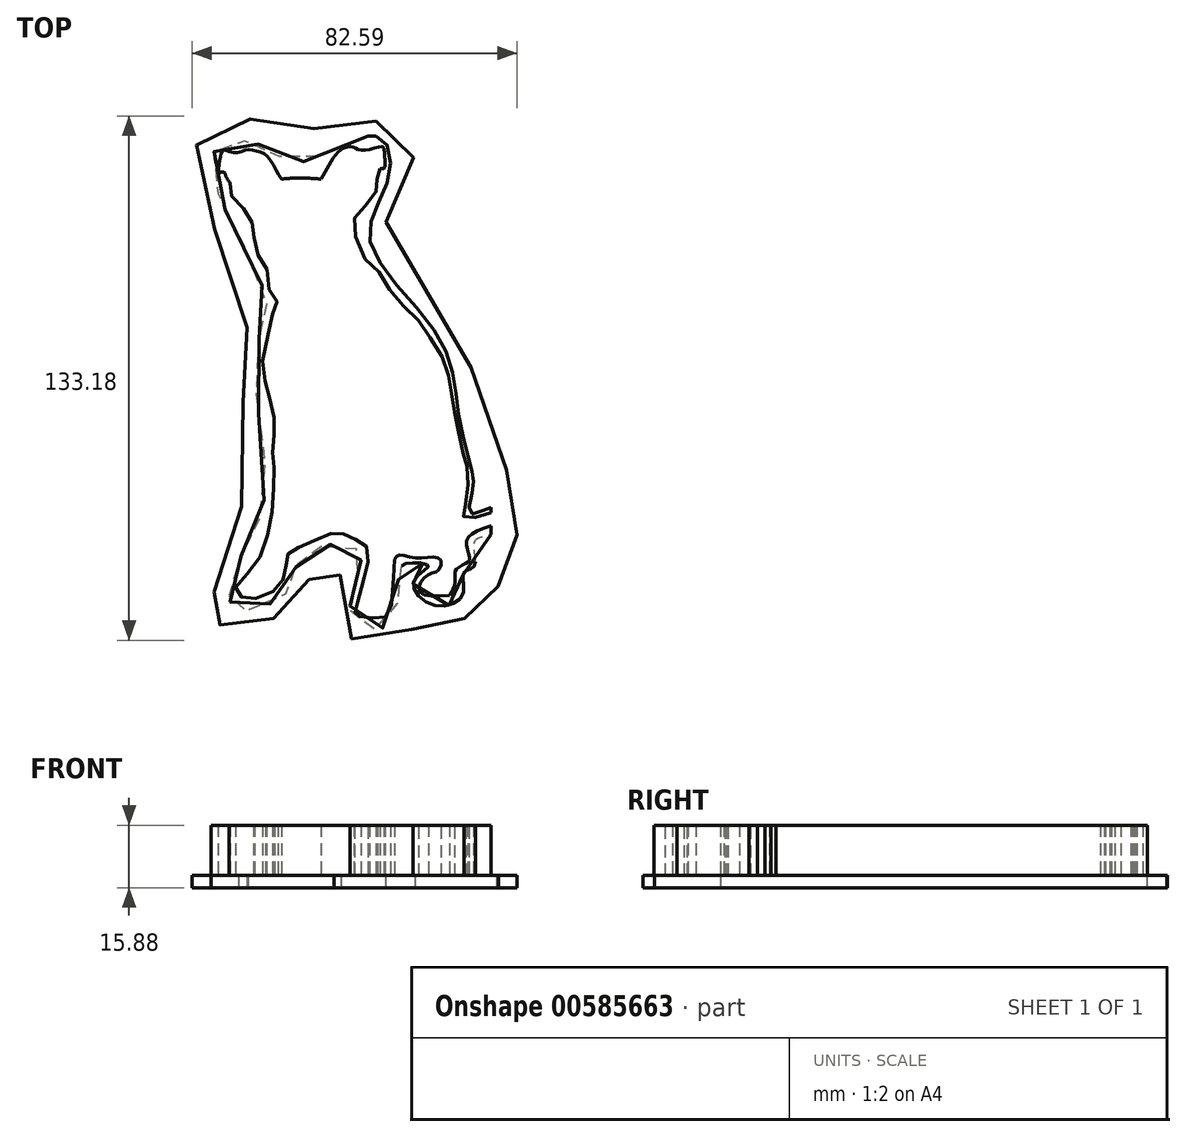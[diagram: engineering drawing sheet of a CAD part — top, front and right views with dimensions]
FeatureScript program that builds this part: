
annotation { "Feature Type Name" : "Feature", "Feature Type Description" : "" }
export const myFeature = defineFeature(function(context is Context, id is Id, definition is map)
    precondition{}
    {
        {
            var Q0;
            Q0=qCreatedBy(makeId("Top.planeOp"),FACE);
            var sketch = newSketch(context, id + "F0", { "sketchPlane" : qUnion([Q0])});
            skLineSegment(sketch, "E0.bottom", {"start": v(38.1, 63.5) * mm, "end": v(-38.1, 63.5) * mm});
            skLineSegment(sketch, "E0.top", {"start": v(38.1, -63.5) * mm, "end": v(-38.1, -63.5) * mm});
            skLineSegment(sketch, "E0.left", {"start": v(38.1, 63.5) * mm, "end": v(38.1, -63.5) * mm});
            skLineSegment(sketch, "E0.right", {"start": v(-38.1, 63.5) * mm, "end": v(-38.1, -63.5) * mm});
            skPoint(sketch, "E0.middle", {"position": v(0, 0) * mm});
            skFitSpline(sketch, "E1", {"points": [v(-26.8, -51.28) * mm, v(-24.47, -48.42) * mm, v(-21, -44.42) * mm, v(-18.8, -38.54) * mm, v(-17.53, -32.17) * mm, v(-17.04, -25.62) * mm, v(-16.95, -20.53) * mm, v(-17.3, -17.93) * mm, v(-17.22, -14.64) * mm, v(-16.87, -11.04) * mm, v(-17.17, -7.08) * mm, v(-18.27, -2.51) * mm, v(-19.15, 1.04) * mm, v(-19.9, 5.22) * mm, v(-18.45, 13.48) * mm, v(-17.35, 18.35) * mm, v(-15.94, 20.72) * mm, v(-17.17, 22.44) * mm, v(-18.27, 24.68) * mm, v(-18.67, 29.46) * mm, v(-20.56, 32.4) * mm, v(-22.05, 36.01) * mm, v(-22.1, 39.52) * mm, v(-22.7, 41.72) * mm, v(-24.17, 44.44) * mm, v(-27.15, 47.31) * mm, v(-28.2, 49.45) * mm, v(-28.2, 51.54) * mm], "startDerivative": vector(59.27, 78.39) * mm, "endDerivative": vector(6.28, 78.17) * mm});
            skFitSpline(sketch, "E2", {"points": [v(-28.2, 51.54) * mm, v(-29.08, 53) * mm, v(-29.7, 54.3) * mm, v(-31.17, 53.97) * mm], "startDerivative": vector(-2.88, 3.86) * mm, "endDerivative": vector(-5.2, -2.35) * mm});
            skFitSpline(sketch, "E3", {"points": [v(-31.17, 53.97) * mm, v(-30.85, 56.65) * mm, v(-30.45, 58.84) * mm, v(-29.9, 59.85) * mm, v(-27.97, 59.37) * mm, v(-25.6, 59.37) * mm, v(-23.7, 60) * mm, v(-21.4, 59.67) * mm, v(-19.33, 58.86) * mm, v(-17.13, 56) * mm, v(-15.12, 52.52) * mm], "startDerivative": vector(2.8, 25.68) * mm, "endDerivative": vector(15.15, -26.64) * mm});
            skFitSpline(sketch, "E4", {"points": [v(-15.12, 52.52) * mm, v(-10.78, 52.82) * mm, v(-5.05, 52.52) * mm], "startDerivative": vector(9, 0.91) * mm, "endDerivative": vector(11.08, -0.87) * mm});
            skFitSpline(sketch, "E5", {"points": [v(-5.05, 52.52) * mm, v(-2.66, 56.77) * mm, v(0, 59.98) * mm, v(2.96, 60.74) * mm, v(5.49, 59.8) * mm, v(10.43, 60.79) * mm, v(11, 60.3) * mm], "startDerivative": vector(11.4, 21.1) * mm, "endDerivative": vector(4.14, -8.3) * mm});
            skFitSpline(sketch, "E6", {"points": [v(11, 60.3) * mm, v(11.15, 57.78) * mm, v(11, 55.3) * mm, v(10.01, 55.23) * mm], "startDerivative": vector(0.31, -6.1) * mm, "endDerivative": vector(-4.87, 1.04) * mm});
            skFitSpline(sketch, "E7", {"points": [v(10.01, 55.23) * mm, v(9.2, 53.36) * mm, v(9.29, 50.86) * mm, v(8.39, 48.27) * mm, v(4.26, 43.68) * mm, v(3.36, 41.77) * mm, v(5.4, 33.2) * mm, v(9.77, 28.85) * mm, v(13.26, 23.1) * mm, v(18.64, 17.83) * mm, v(22.49, 12.64) * mm, v(26.42, 5.83) * mm, v(27.78, 0.19) * mm, v(28.58, -5.18) * mm, v(29.87, -11.33) * mm, v(31.3, -18.15) * mm, v(32.04, -20.73) * mm, v(32.19, -26.72) * mm, v(31.37, -31.45) * mm, v(31.3, -33.37) * mm, v(33.4, -33.62) * mm, v(36.62, -32.74) * mm, v(43.28, -30.45) * mm], "startDerivative": vector(-36.05, -59.29) * mm, "endDerivative": vector(133.24, 45.56) * mm});
            skFitSpline(sketch, "E8", {"points": [v(-26.8, -51.28) * mm, v(-24.66, -54) * mm, v(-17.08, -52.08) * mm, v(-14.04, -46.92) * mm, v(-13.48, -42.76) * mm, v(-8.7, -40.27) * mm, v(-1.18, -37.23) * mm, v(2.73, -38.66) * mm, v(6.77, -41.27) * mm, v(5.96, -48.66) * mm, v(5.28, -51.28) * mm, v(3.67, -56.86) * mm, v(3.6, -57.8) * mm, v(4.66, -58.6) * mm, v(10.01, -58.97) * mm, v(12.49, -57.42) * mm, v(13.67, -44.17) * mm], "startDerivative": vector(26.44, -66.46) * mm, "endDerivative": vector(8.54, 33.09) * mm});
            skFitSpline(sketch, "E9", {"points": [v(13.67, -44.17) * mm, v(14.6, -43.06) * mm, v(17.82, -43.57) * mm, v(22.55, -43.58) * mm, v(25.32, -44.17) * mm, v(24.95, -46.75) * mm, v(23, -47.64) * mm, v(20.56, -49.49) * mm, v(20.15, -52.48) * mm, v(27.61, -53.26) * mm], "startDerivative": vector(9.44, 19.23) * mm, "endDerivative": vector(57.92, 3.55) * mm});
            skFitSpline(sketch, "E10", {"points": [v(27.61, -53.26) * mm, v(29.02, -49.86) * mm, v(29.2, -46.75) * mm, v(31.86, -45.06) * mm, v(32.67, -43.54) * mm, v(32, -39.1) * mm, v(43.28, -34.27) * mm], "startDerivative": vector(12.68, 21.26) * mm, "endDerivative": vector(55.35, 13.04) * mm});
            skLineSegment(sketch, "E11", {"start": v(38.1, -32.42) * mm, "end": v(38.1, -35.48) * mm});
            skFitSpline(sketch, "E12", {"points": [v(37.2, -31.13) * mm, v(32.96, -32.5) * mm, v(33.54, -26.22) * mm, v(33.36, -21.87) * mm, v(29.84, -6.64) * mm, v(24.91, 12.37) * mm, v(7.38, 37.17) * mm, v(12.28, 53.45) * mm, v(8.94, 63.5) * mm, v(-10.47, 56.8) * mm, v(-20.58, 61.23) * mm, v(-31.37, 60.62) * mm, v(-30.9, 48.08) * mm, v(-18.86, 20.67) * mm, v(-21.82, 7.6) * mm, v(-19.2, -26.9) * mm, v(-25.56, -43.68) * mm, v(-28.27, -54.4) * mm, v(-24.54, -57.22) * mm, v(-12.06, -50.64) * mm, v(-10.8, -43.95) * mm, v(-0.9, -40.24) * mm, v(4.92, -42.75) * mm, v(3.17, -50.63) * mm, v(3.95, -60.24) * mm, v(12.93, -60.03) * mm, v(14.93, -46.74) * mm, v(18.18, -44.99) * mm, v(22.23, -45.84) * mm, v(18.5, -49.66) * mm, v(23.7, -55.8) * mm, v(30.97, -52.96) * mm, v(31.13, -47.64) * mm, v(32.87, -46.57) * mm, v(34.18, -44.78) * mm, v(34.21, -39.16) * mm, v(38.77, -37.33) * mm, v(39.07, -33.43) * mm, v(38.37, -31.11) * mm, v(37.2, -31.13) * mm]});
            skPoint(sketch, "E13.visualSharp", {"position": v(38.1, -32.23) * mm});
            skArc(sketch, "E13.filletArc", {"start": v(38.1, -32.42) * mm, "mid": v(38.04, -32.3) * mm, "end": v(37.92, -32.29) * mm});
            skPoint(sketch, "E14.visualSharp", {"position": v(38.1, -35.58) * mm});
            skArc(sketch, "E14.filletArc", {"start": v(38, -35.6) * mm, "mid": v(38.07, -35.56) * mm, "end": v(38.1, -35.48) * mm});
            skSolve(sketch);
        }
        {
            var Q0;
            Q0=sQuery(id+"F0.wireOp",EDGE,"E4");
            var Q1;
            Q1=sQuery(id+"F0.wireOp",EDGE,"E5");
            var Q2;
            Q2=sQuery(id+"F0.wireOp",EDGE,"E6");
            var Q3;
            Q3=sQuery(id+"F0.wireOp",EDGE,"E1");
            var Q4;
            Q4=sQuery(id+"F0.wireOp",EDGE,"E9");
            var Q5;
            Q5=sQuery(id+"F0.wireOp",EDGE,"E10");
            var Q6;
            Q6=sQuery(id+"F0.wireOp",EDGE,"E8");
            var Q7;
            Q7=sQuery(id+"F0.wireOp",EDGE,"E3");
            var Q8;
            Q8=sQuery(id+"F0.wireOp",EDGE,"E11");
            var Q9;
            Q9=sQuery(id+"F0.wireOp",EDGE,"E2");
            var Q10;
            Q10=sQuery(id+"F0.wireOp",EDGE,"E7");
            extrude(context, id + "F1", {"bodyType" : ToolBodyType.SURFACE, "surfaceEntities" : qUnion([Q0, Q1, Q2, Q3, Q4, Q5, Q6, Q7, Q8, Q9, Q10]), "depth" : 12.7 * mm, "offsetDistance" : 25.4 * mm});
        }
        {
            var Q0;
            Q0=makeQuery(id+"F0.imprint","IMPRINT",FACE,{"disambiguationData":[TD([[makeQuery(id+"F0.imprint","IMPRINT",EDGE,{"derivedFrom":sQuery(id+"F0.wireOp",EDGE,"E1")}),1.0]])]});
            var Q1;
            {var subQ0=sQuery(id+"F0.wireOp",EDGE,"E11");Q1=makeQuery(id+"F0.imprint","IMPRINT",FACE,{"disambiguationData":[TD([[makeQuery(id+"F0.imprint","IMPRINT",EDGE,{"derivedFrom":subQ0}),1.0]])]});}
            extrude(context, id + "F2", {"entities" : qUnion([Q0, Q1]), "depth" : 12.7 * mm, "offsetDistance" : 25.4 * mm});
        }
        {
            var Q0;
            Q0=makeQuery(id+"F2.opExtrude","CAP_FACE",FACE,{"disambiguationData":[OSD([sQuery(id+"F0.wireOp",EDGE,"E0.bottom"),sQuery(id+"F0.wireOp",EDGE,"E1"),sQuery(id+"F0.wireOp",EDGE,"E2"),sQuery(id+"F0.wireOp",EDGE,"E3"),sQuery(id+"F0.wireOp",EDGE,"E4"),sQuery(id+"F0.wireOp",EDGE,"E5"),sQuery(id+"F0.wireOp",EDGE,"E6"),sQuery(id+"F0.wireOp",EDGE,"E7"),sQuery(id+"F0.wireOp",EDGE,"E8"),sQuery(id+"F0.wireOp",EDGE,"E9"),sQuery(id+"F0.wireOp",EDGE,"E10"),sQuery(id+"F0.wireOp",EDGE,"E11"),sQuery(id+"F0.wireOp",EDGE,"E12")])],"isStart":true});
            var sketch = newSketch(context, id + "F3", { "sketchPlane" : qUnion([Q0])});
            skFitSpline(sketch, "E15", {"points": [v(8.94, -67.25) * mm, v(-1.23, -67.8) * mm, v(-13.7, -63.5) * mm, v(-25.28, -68.45) * mm, v(-35.13, -63.5) * mm, v(-37.13, -51.85) * mm, v(-23.84, -19.78) * mm, v(-25.8, -5.64) * mm, v(-23.41, 17.83) * mm, v(-30.14, 46.47) * mm, v(-32.92, 55.71) * mm, v(-32.35, 58.1) * mm, v(-30.85, 60.6) * mm, v(-29.37, 61.5) * mm, v(-18.43, 59.45) * mm, v(-9.5, 55.54) * mm, v(-6.72, 46.6) * mm, v(0, 45.57) * mm, v(-1.7, 53.32) * mm, v(2.99, 64.53) * mm, v(4.76, 64.08) * mm, v(19.98, 61.74) * mm, v(22.8, 61.59) * mm, v(35.4, 57.93) * mm, v(39.95, 55.24) * mm, v(39.97, 45.8) * mm, v(44.34, 39.58) * mm, v(42.65, 23.22) * mm, v(41.77, 20.62) * mm, v(27.77, -16.6) * mm, v(15.82, -31.78) * mm, v(11.45, -40.67) * mm, v(16.16, -53.31) * mm, v(18.57, -61.96) * mm, v(8.94, -67.25) * mm]});
            skSolve(sketch);
        }
        {
            var Q0;
            Q0=makeQuery(id+"F3.imprint","IMPRINT",FACE,{"disambiguationData":[TD([[makeQuery(id+"F3.imprint","IMPRINT",EDGE,{"derivedFrom":sQuery(id+"F3.wireOp",EDGE,"E15")}),-1.0]])]});
            var Q1;
            Q1=makeQuery(id+"F3.imprint","IMPRINT",FACE,{"disambiguationData":[TD([[makeQuery(id+"F3.imprint","IMPRINT",EDGE,{"derivedFrom":makeQuery(id+"F2.opExtrude","CAP_EDGE",EDGE,{"disambiguationData":[OSD([sQuery(id+"F0.wireOp",EDGE,"E0.bottom")])],"isStart":true})}),-1.0]])]});
            extrude(context, id + "F4", {"entities" : qUnion([Q0, Q1]), "operationType" : NewBodyOperationType.ADD, "depth" : 3.17 * mm, "offsetDistance" : 25.4 * mm});
        }
    });
